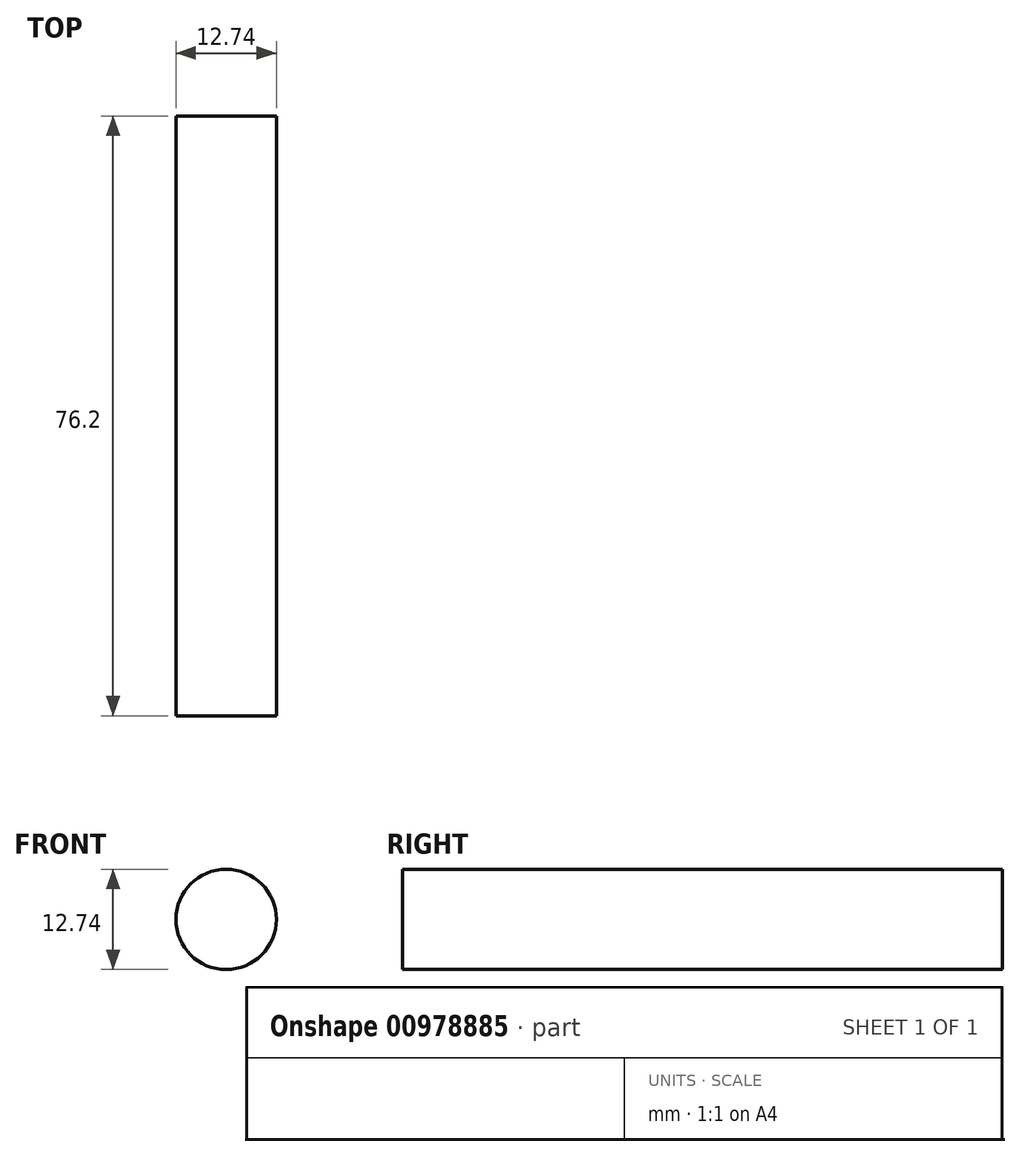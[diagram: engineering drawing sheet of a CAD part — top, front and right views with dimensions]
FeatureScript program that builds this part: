
annotation { "Feature Type Name" : "Feature", "Feature Type Description" : "" }
export const myFeature = defineFeature(function(context is Context, id is Id, definition is map)
    precondition{}
    {
        {
            var Q0;
            Q0=qCreatedBy(makeId("Front.planeOp"),FACE);
            var sketch = newSketch(context, id + "F0", { "sketchPlane" : qUnion([Q0])});
            skCircle(sketch, "E0", {"center": v(0, 0) * mm, "radius": 6.37 * mm});
            skSolve(sketch);
        }
        {
            var Q0;
            Q0=makeQuery(id+"F0.imprint","IMPRINT",FACE,{"disambiguationData":[TD([[makeQuery(id+"F0.imprint","IMPRINT",EDGE,{"derivedFrom":sQuery(id+"F0.wireOp",EDGE,"E0")}),1.0]])]});
            extrude(context, id + "F1", {"entities" : qUnion([Q0]), "depth" : 76.2 * mm, "offsetDistance" : 25.4 * mm});
        }
    });
